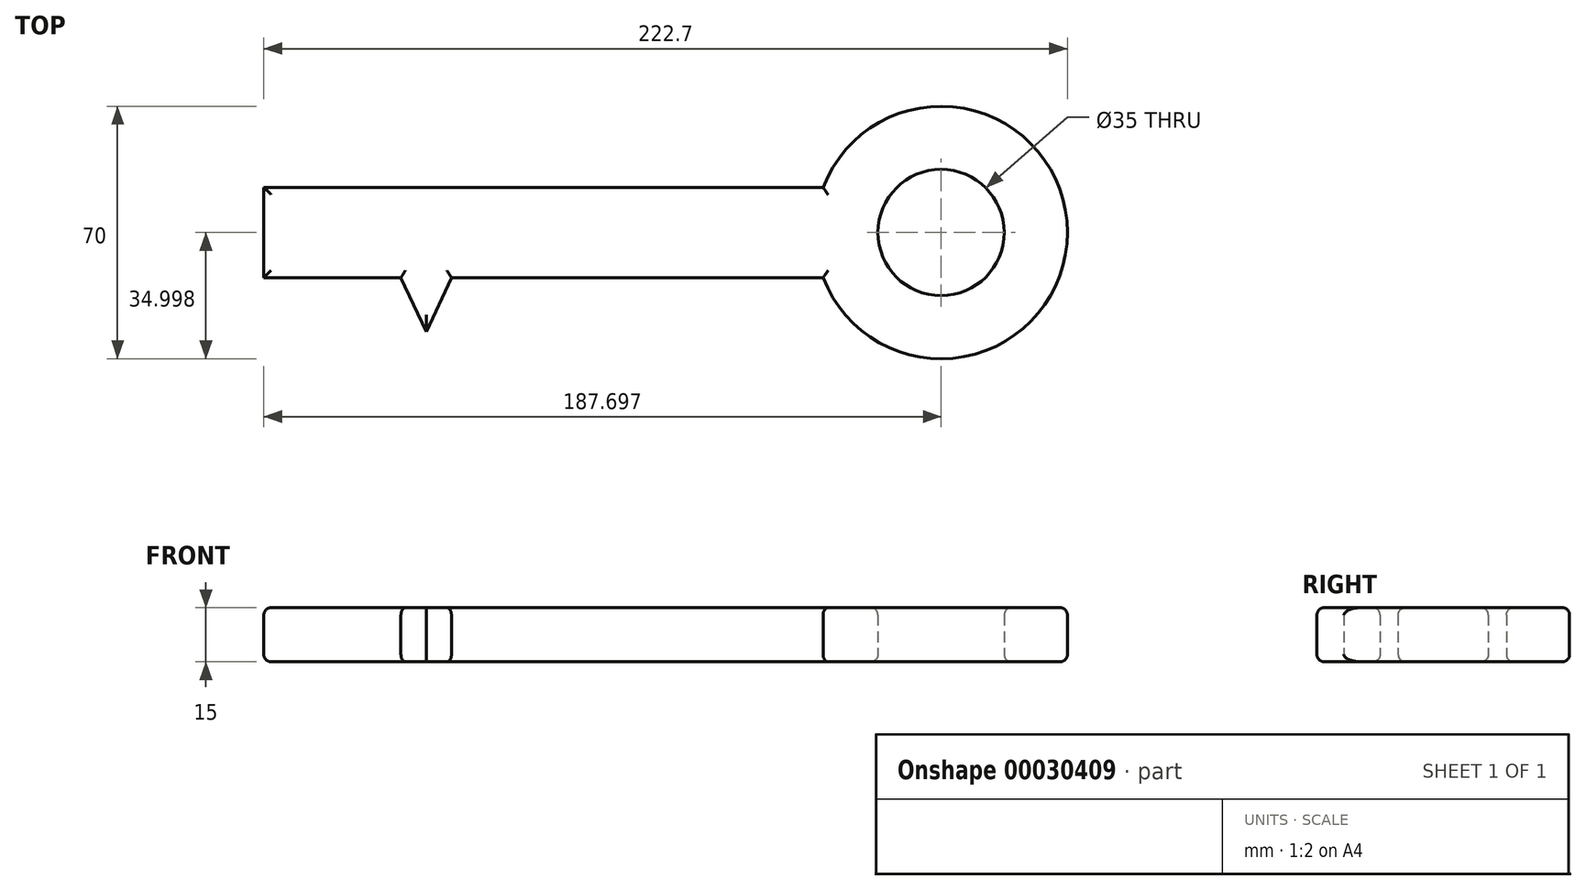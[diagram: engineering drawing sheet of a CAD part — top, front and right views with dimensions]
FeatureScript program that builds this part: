
annotation { "Feature Type Name" : "Feature", "Feature Type Description" : "" }
export const myFeature = defineFeature(function(context is Context, id is Id, definition is map)
    precondition{}
    {
        {
            var Q0;
            Q0=qCreatedBy(makeId("Top.planeOp"),FACE);
            var sketch = newSketch(context, id + "F0", { "sketchPlane" : qUnion([Q0])});
            skLineSegment(sketch, "E0.bottom", {"start": v(13.38, 23.13) * mm, "end": v(-141.62, 23.13) * mm});
            skLineSegment(sketch, "E0.top", {"start": v(13.38, -1.87) * mm, "end": v(-141.62, -1.87) * mm});
            skLineSegment(sketch, "E0.right", {"start": v(-141.62, 23.13) * mm, "end": v(-141.62, -1.87) * mm});
            skLineSegment(sketch, "E1.bottom", {"start": v(-141.62, -1.87) * mm, "end": v(-131.62, -1.87) * mm});
            skLineSegment(sketch, "E1.top", {"start": v(-141.62, -31.87) * mm, "end": v(-131.62, -31.87) * mm});
            skLineSegment(sketch, "E1.left", {"start": v(-141.62, -1.87) * mm, "end": v(-141.62, -31.87) * mm});
            skLineSegment(sketch, "E1.right", {"start": v(-131.62, -1.87) * mm, "end": v(-131.62, -31.87) * mm});
            skLineSegment(sketch, "E2.bottom", {"start": v(-121.62, -1.87) * mm, "end": v(-113.62, -1.87) * mm});
            skLineSegment(sketch, "E2.top", {"start": v(-121.62, -16.87) * mm, "end": v(-113.62, -16.87) * mm});
            skLineSegment(sketch, "E2.left", {"start": v(-121.62, -1.87) * mm, "end": v(-121.62, -16.87) * mm});
            skLineSegment(sketch, "E2.right", {"start": v(-113.62, -1.87) * mm, "end": v(-113.62, -16.87) * mm});
            skLineSegment(sketch, "E3", {"start": v(-103.62, -1.87) * mm, "end": v(-96.62, -16.87) * mm});
            skLineSegment(sketch, "E4", {"start": v(-96.62, -16.87) * mm, "end": v(-89.62, -1.87) * mm});
            skPoint(sketch, "E5", {"position": v(-96.62, -1.87) * mm});
            skArc(sketch, "E6", {"start": v(13.38, -1.87) * mm, "mid": v(81.08, 10.63) * mm, "end": v(13.38, 23.13) * mm});
            skCircle(sketch, "E7", {"center": v(46.08, 10.63) * mm, "radius": 17.5 * mm});
            skLineSegment(sketch, "E8", {"start": v(-141.62, 10.63) * mm, "end": v(46.08, 10.63) * mm, "construction": true});
            skSolve(sketch);
        }
        {
            var Q0;
            Q0=makeQuery(id+"F0.imprint","IMPRINT",FACE,{"disambiguationData":[TD([[makeQuery(id+"F0.imprint","IMPRINT",EDGE,{"derivedFrom":sQuery(id+"F0.wireOp",EDGE,"E0.bottom")}),1.0]])]});
            var Q1;
            Q1=makeQuery(id+"F0.imprint","IMPRINT",FACE,{"disambiguationData":[TD([[makeQuery(id+"F0.imprint","IMPRINT",EDGE,{"derivedFrom":sQuery(id+"F0.wireOp",EDGE,"E1.bottom")}),-1.0]])]});
            var Q2;
            Q2=makeQuery(id+"F0.imprint","IMPRINT",FACE,{"disambiguationData":[TD([[makeQuery(id+"F0.imprint","IMPRINT",EDGE,{"derivedFrom":sQuery(id+"F0.wireOp",EDGE,"E2.bottom")}),-1.0]])]});
            var Q3;
            {var subQ1=sQuery(id+"F0.wireOp",EDGE,"E3");Q3=makeQuery(id+"F0.imprint","IMPRINT",FACE,{"disambiguationData":[TD([[makeQuery(id+"F0.imprint","IMPRINT",EDGE,{"derivedFrom":subQ1}),1.0]])]});}
            extrude(context, id + "F1", {"entities" : qUnion([Q0, Q1, Q2, Q3]), "depth" : 15 * mm});
        }
        {
            var Q0;
            Q0=makeQuery(id+"F1.opExtrude","CAP_EDGE",EDGE,{"disambiguationData":[OSD([sQuery(id+"F0.wireOp",EDGE,"E7")])],"isStart":false});
            var Q1;
            Q1=makeQuery(id+"F1.opExtrude","CAP_EDGE",EDGE,{"disambiguationData":[OSD([sQuery(id+"F0.wireOp",EDGE,"E6")])],"isStart":false});
            var Q2;
            Q2=makeQuery(id+"F1.opExtrude","CAP_EDGE",EDGE,{"disambiguationData":[OSD([sQuery(id+"F0.wireOp",EDGE,"E0.bottom")])],"isStart":false});
            var Q3;
            {var subQ0=sQuery(id+"F0.wireOp",EDGE,"E0.top");Q3=makeQuery(id+"F1.opExtrude","CAP_EDGE",EDGE,{"disambiguationData":[OSD([subQ0]),TDD([makeQuery(id+"F0.imprint","IMPRINT",EDGE,{"disambiguationData":[TD([[makeQuery(id+"F0.imprint","INTERSECT",VERTEX,{"derivedFrom":[subQ0,sQuery(id+"F0.wireOp",EDGE,"E6")]}),-1.0]])],"derivedFrom":subQ0})])],"isStart":false});}
            var Q4;
            Q4=makeQuery(id+"F1.opExtrude","CAP_EDGE",EDGE,{"disambiguationData":[OSD([sQuery(id+"F0.wireOp",EDGE,"E4")])],"isStart":false});
            var Q5;
            {var subQ0=sQuery(id+"F0.wireOp",EDGE,"E0.top");Q5=makeQuery(id+"F1.opExtrude","CAP_EDGE",EDGE,{"disambiguationData":[OSD([subQ0]),TDD([makeQuery(id+"F0.imprint","IMPRINT",EDGE,{"disambiguationData":[TD([[makeQuery(id+"F0.imprint","INTERSECT",VERTEX,{"derivedFrom":[subQ0,sQuery(id+"F0.wireOp",EDGE,"E3")]}),-1.0]])],"derivedFrom":subQ0})])],"isStart":false});}
            var Q6;
            Q6=makeQuery(id+"F1.opExtrude","CAP_EDGE",EDGE,{"disambiguationData":[OSD([sQuery(id+"F0.wireOp",EDGE,"E2.right")])],"isStart":false});
            var Q7;
            Q7=makeQuery(id+"F1.opExtrude","CAP_EDGE",EDGE,{"disambiguationData":[OSD([sQuery(id+"F0.wireOp",EDGE,"E2.top")])],"isStart":false});
            var Q8;
            Q8=makeQuery(id+"F1.opExtrude","CAP_EDGE",EDGE,{"disambiguationData":[OSD([sQuery(id+"F0.wireOp",EDGE,"E3")])],"isStart":false});
            var Q9;
            {var subQ0=sQuery(id+"F0.wireOp",EDGE,"E0.top");Q9=makeQuery(id+"F1.opExtrude","CAP_EDGE",EDGE,{"disambiguationData":[OSD([subQ0]),TDD([makeQuery(id+"F0.imprint","IMPRINT",EDGE,{"disambiguationData":[TD([[makeQuery(id+"F0.imprint","INTERSECT",VERTEX,{"derivedFrom":[subQ0,sQuery(id+"F0.wireOp",EDGE,"E1.bottom"),sQuery(id+"F0.wireOp",EDGE,"E1.right")]}),1.0]])],"derivedFrom":subQ0})])],"isStart":false});}
            var Q10;
            Q10=makeQuery(id+"F1.opExtrude","CAP_EDGE",EDGE,{"disambiguationData":[OSD([sQuery(id+"F0.wireOp",EDGE,"E2.left")])],"isStart":false});
            var Q11;
            Q11=makeQuery(id+"F1.opExtrude","CAP_EDGE",EDGE,{"disambiguationData":[OSD([sQuery(id+"F0.wireOp",EDGE,"E1.right")])],"isStart":false});
            var Q12;
            Q12=makeQuery(id+"F1.opExtrude","CAP_FACE",FACE,{"disambiguationData":[OSD([sQuery(id+"F0.wireOp",EDGE,"E0.bottom"),sQuery(id+"F0.wireOp",EDGE,"E0.top"),sQuery(id+"F0.wireOp",EDGE,"E0.right"),sQuery(id+"F0.wireOp",EDGE,"E1.top"),sQuery(id+"F0.wireOp",EDGE,"E1.left"),sQuery(id+"F0.wireOp",EDGE,"E1.right"),sQuery(id+"F0.wireOp",EDGE,"E2.top"),sQuery(id+"F0.wireOp",EDGE,"E2.left"),sQuery(id+"F0.wireOp",EDGE,"E2.right"),sQuery(id+"F0.wireOp",EDGE,"E3"),sQuery(id+"F0.wireOp",EDGE,"E4"),sQuery(id+"F0.wireOp",EDGE,"E6"),sQuery(id+"F0.wireOp",EDGE,"E7")])],"isStart":false});
            var Q13;
            Q13=makeQuery(id+"F1.opExtrude","CAP_EDGE",EDGE,{"disambiguationData":[OSD([sQuery(id+"F0.wireOp",EDGE,"E0.right"),sQuery(id+"F0.wireOp",EDGE,"E1.left")])],"isStart":false});
            var Q14;
            Q14=makeQuery(id+"F1.opExtrude","CAP_EDGE",EDGE,{"disambiguationData":[OSD([sQuery(id+"F0.wireOp",EDGE,"E7")])],"isStart":true});
            var Q15;
            Q15=makeQuery(id+"F1.opExtrude","CAP_EDGE",EDGE,{"disambiguationData":[OSD([sQuery(id+"F0.wireOp",EDGE,"E4")])],"isStart":true});
            var Q16;
            Q16=makeQuery(id+"F1.opExtrude","CAP_EDGE",EDGE,{"disambiguationData":[OSD([sQuery(id+"F0.wireOp",EDGE,"E3")])],"isStart":true});
            var Q17;
            {var subQ0=sQuery(id+"F0.wireOp",EDGE,"E0.top");Q17=makeQuery(id+"F1.opExtrude","CAP_EDGE",EDGE,{"disambiguationData":[OSD([subQ0]),TDD([makeQuery(id+"F0.imprint","IMPRINT",EDGE,{"disambiguationData":[TD([[makeQuery(id+"F0.imprint","INTERSECT",VERTEX,{"derivedFrom":[subQ0,sQuery(id+"F0.wireOp",EDGE,"E6")]}),-1.0]])],"derivedFrom":subQ0})])],"isStart":true});}
            var Q18;
            Q18=makeQuery(id+"F1.opExtrude","CAP_EDGE",EDGE,{"disambiguationData":[OSD([sQuery(id+"F0.wireOp",EDGE,"E0.right"),sQuery(id+"F0.wireOp",EDGE,"E1.left")])],"isStart":true});
            var Q19;
            Q19=makeQuery(id+"F1.opExtrude","CAP_EDGE",EDGE,{"disambiguationData":[OSD([sQuery(id+"F0.wireOp",EDGE,"E0.bottom")])],"isStart":true});
            var Q20;
            Q20=makeQuery(id+"F1.opExtrude","CAP_EDGE",EDGE,{"disambiguationData":[OSD([sQuery(id+"F0.wireOp",EDGE,"E6")])],"isStart":true});
            var Q21;
            Q21=makeQuery(id+"F1.opExtrude","CAP_EDGE",EDGE,{"disambiguationData":[OSD([sQuery(id+"F0.wireOp",EDGE,"E2.top")])],"isStart":true});
            var Q22;
            Q22=makeQuery(id+"F1.opExtrude","CAP_EDGE",EDGE,{"disambiguationData":[OSD([sQuery(id+"F0.wireOp",EDGE,"E1.top")])],"isStart":true});
            var Q23;
            {var subQ0=sQuery(id+"F0.wireOp",EDGE,"E0.top");Q23=makeQuery(id+"F1.opExtrude","CAP_EDGE",EDGE,{"disambiguationData":[OSD([subQ0]),TDD([makeQuery(id+"F0.imprint","IMPRINT",EDGE,{"disambiguationData":[TD([[makeQuery(id+"F0.imprint","INTERSECT",VERTEX,{"derivedFrom":[subQ0,sQuery(id+"F0.wireOp",EDGE,"E1.bottom"),sQuery(id+"F0.wireOp",EDGE,"E1.right")]}),1.0]])],"derivedFrom":subQ0})])],"isStart":true});}
            var Q24;
            {var subQ0=sQuery(id+"F0.wireOp",EDGE,"E0.top");Q24=makeQuery(id+"F1.opExtrude","CAP_EDGE",EDGE,{"disambiguationData":[OSD([subQ0]),TDD([makeQuery(id+"F0.imprint","IMPRINT",EDGE,{"disambiguationData":[TD([[makeQuery(id+"F0.imprint","INTERSECT",VERTEX,{"derivedFrom":[subQ0,sQuery(id+"F0.wireOp",EDGE,"E3")]}),-1.0]])],"derivedFrom":subQ0})])],"isStart":true});}
            var Q25;
            Q25=makeQuery(id+"F1.opExtrude","CAP_EDGE",EDGE,{"disambiguationData":[OSD([sQuery(id+"F0.wireOp",EDGE,"E2.right")])],"isStart":true});
            var Q26;
            Q26=makeQuery(id+"F1.opExtrude","CAP_EDGE",EDGE,{"disambiguationData":[OSD([sQuery(id+"F0.wireOp",EDGE,"E1.right")])],"isStart":true});
            var Q27;
            Q27=makeQuery(id+"F1.opExtrude","CAP_EDGE",EDGE,{"disambiguationData":[OSD([sQuery(id+"F0.wireOp",EDGE,"E2.left")])],"isStart":true});
            fillet(context, id + "F2", {"entities" : qUnion([Q0, Q1, Q2, Q3, Q4, Q5, Q6, Q7, Q8, Q9, Q10, Q11, Q12, Q13, Q14, Q15, Q16, Q17, Q18, Q19, Q20, Q21, Q22, Q23, Q24, Q25, Q26, Q27]), "radius" : 2 * mm, "tangentPropagation" : true, "allowEdgeOverflow" : false});
        }
    });
